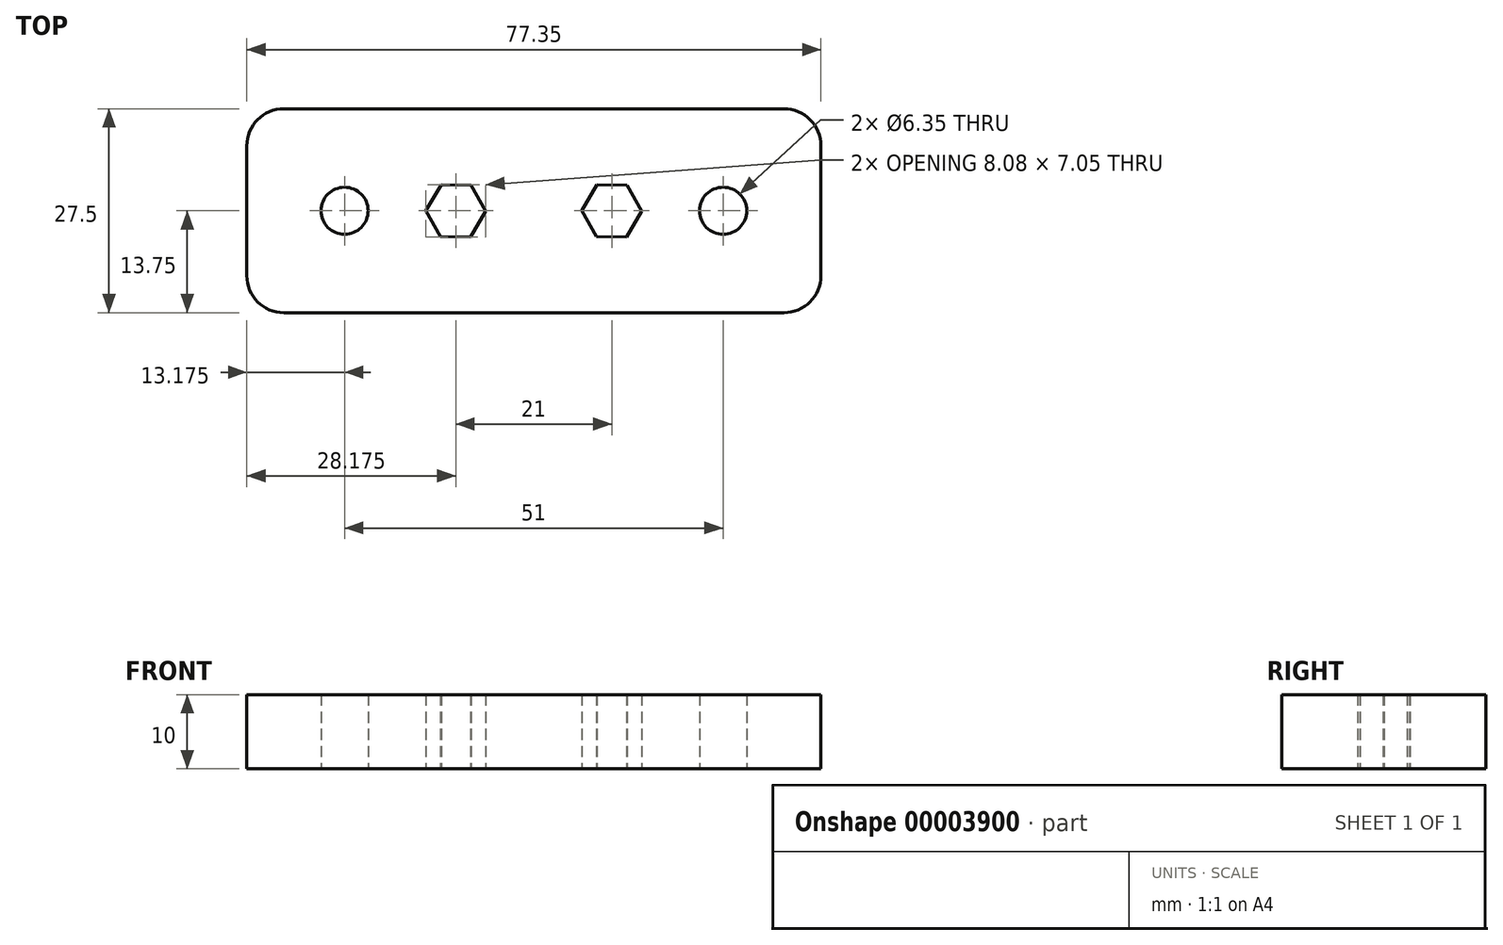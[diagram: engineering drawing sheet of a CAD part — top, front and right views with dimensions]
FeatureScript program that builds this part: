
annotation { "Feature Type Name" : "Feature", "Feature Type Description" : "" }
export const myFeature = defineFeature(function(context is Context, id is Id, definition is map)
    precondition{}
    {
        {
            var Q0;
            Q0=qCreatedBy(makeId("Top.planeOp"),FACE);
            var sketch = newSketch(context, id + "F0", { "sketchPlane" : qUnion([Q0])});
            skCircle(sketch, "E0", {"center": v(10.65, 0) * mm, "radius": 3.17 * mm});
            skCircle(sketch, "E1", {"center": v(61.65, 0) * mm, "radius": 3.17 * mm});
            skLineSegment(sketch, "E2", {"start": v(13.82, 21.74) * mm, "end": v(13.82, -22) * mm, "construction": true});
            skLineSegment(sketch, "E3", {"start": v(58.47, 21.74) * mm, "end": v(58.47, -22) * mm, "construction": true});
            skLineSegment(sketch, "E4", {"start": v(25.65, 0) * mm, "end": v(46.65, 0) * mm, "construction": true});
            skLineSegment(sketch, "E5", {"start": v(46.65, 0) * mm, "end": v(61.65, 0) * mm, "construction": true});
            skLineSegment(sketch, "E6", {"start": v(10.65, 0) * mm, "end": v(25.65, 0) * mm, "construction": true});
            skLineSegment(sketch, "E7", {"start": v(13.82, 21.74) * mm, "end": v(58.47, 21.74) * mm, "construction": true});
            skLineSegment(sketch, "E8", {"start": v(13.82, -22) * mm, "end": v(58.47, -22) * mm, "construction": true});
            skCircle(sketch, "E9.cCircle", {"center": v(25.65, 0) * mm, "radius": 3.5 * mm, "construction": true});
            skLineSegment(sketch, "E9.0", {"start": v(27.7, 3.48) * mm, "end": v(29.69, -0.05) * mm});
            skLineSegment(sketch, "E9.1", {"start": v(29.69, -0.05) * mm, "end": v(27.62, -3.52) * mm});
            skLineSegment(sketch, "E9.2", {"start": v(27.62, -3.52) * mm, "end": v(23.58, -3.48) * mm});
            skLineSegment(sketch, "E9.3", {"start": v(23.58, -3.48) * mm, "end": v(21.6, 0.05) * mm});
            skLineSegment(sketch, "E9.4", {"start": v(21.6, 0.05) * mm, "end": v(23.67, 3.52) * mm});
            skLineSegment(sketch, "E9.5", {"start": v(23.67, 3.52) * mm, "end": v(27.7, 3.48) * mm});
            skPoint(sketch, "E9.0.midPoint", {"position": v(28.7, 1.71) * mm});
            skCircle(sketch, "E10.cCircle", {"center": v(46.65, 0) * mm, "radius": 3.5 * mm, "construction": true});
            skLineSegment(sketch, "E10.0", {"start": v(48.7, 3.48) * mm, "end": v(50.69, -0.05) * mm});
            skLineSegment(sketch, "E10.1", {"start": v(50.69, -0.05) * mm, "end": v(48.62, -3.52) * mm});
            skLineSegment(sketch, "E10.2", {"start": v(48.62, -3.52) * mm, "end": v(44.58, -3.48) * mm});
            skLineSegment(sketch, "E10.3", {"start": v(44.58, -3.48) * mm, "end": v(42.6, 0.05) * mm});
            skLineSegment(sketch, "E10.4", {"start": v(42.6, 0.05) * mm, "end": v(44.67, 3.52) * mm});
            skLineSegment(sketch, "E10.5", {"start": v(44.67, 3.52) * mm, "end": v(48.7, 3.48) * mm});
            skPoint(sketch, "E10.0.midPoint", {"position": v(49.7, 1.71) * mm});
            skLineSegment(sketch, "E11.rect.bottom", {"start": v(74.82, 13.75) * mm, "end": v(-2.53, 13.75) * mm});
            skLineSegment(sketch, "E11.rect.top", {"start": v(74.82, -13.75) * mm, "end": v(-2.53, -13.75) * mm});
            skLineSegment(sketch, "E11.rect.left", {"start": v(74.82, 13.75) * mm, "end": v(74.82, -13.75) * mm});
            skLineSegment(sketch, "E11.rect.right", {"start": v(-2.53, 13.75) * mm, "end": v(-2.53, -13.75) * mm});
            skPoint(sketch, "E11.rect.middle", {"position": v(36.15, 0) * mm});
            skLineSegment(sketch, "E12", {"start": v(7.47, 0) * mm, "end": v(-2.53, 0) * mm, "construction": true});
            skSolve(sketch);
        }
        {
            var Q0;
            Q0=makeQuery(id+"F0.imprint","IMPRINT",FACE,{"disambiguationData":[TD([[makeQuery(id+"F0.imprint","IMPRINT",EDGE,{"derivedFrom":sQuery(id+"F0.wireOp",EDGE,"E0")}),-1.0]])]});
            extrude(context, id + "F1", {"entities" : qUnion([Q0]), "depth" : 10 * mm});
        }
        {
            var Q0;
            Q0=makeQuery(id+"F1.opExtrude","SWEPT_EDGE",EDGE,{"disambiguationData":[OSD([sQuery(id+"F0.wireOp",EDGE,"E11.rect.bottom"),sQuery(id+"F0.wireOp",EDGE,"E11.rect.right")])]});
            var Q1;
            Q1=makeQuery(id+"F1.opExtrude","SWEPT_EDGE",EDGE,{"disambiguationData":[OSD([sQuery(id+"F0.wireOp",EDGE,"E11.rect.top"),sQuery(id+"F0.wireOp",EDGE,"E11.rect.right")])]});
            var Q2;
            Q2=makeQuery(id+"F1.opExtrude","SWEPT_EDGE",EDGE,{"disambiguationData":[OSD([sQuery(id+"F0.wireOp",EDGE,"E11.rect.top"),sQuery(id+"F0.wireOp",EDGE,"E11.rect.left")])]});
            var Q3;
            Q3=makeQuery(id+"F1.opExtrude","SWEPT_EDGE",EDGE,{"disambiguationData":[OSD([sQuery(id+"F0.wireOp",EDGE,"E11.rect.bottom"),sQuery(id+"F0.wireOp",EDGE,"E11.rect.left")])]});
            fillet(context, id + "F2", {"entities" : qUnion([Q0, Q1, Q2, Q3]), "radius" : 5 * mm, "tangentPropagation" : true, "allowEdgeOverflow" : false});
        }
    });
